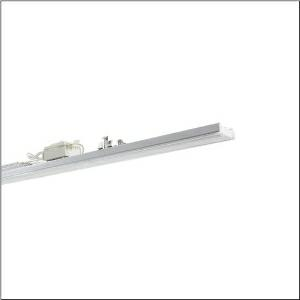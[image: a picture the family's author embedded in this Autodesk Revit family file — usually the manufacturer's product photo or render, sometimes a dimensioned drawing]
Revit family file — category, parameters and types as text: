
# Revit family: licross_21_recessed_ho_52tl11dn4e5s
name_source: partatom
category: Lighting Fixtures
units: mm (PartAtom-declared; Revit-internal decimal feet)

## family parameters
Cut with Voids When Loaded = No
Host = Face
Light Source = No
Part Type = Normal
Room Calculation Point = No
Round Connector Dimension = Use Diameter
Shared = No

## types (1)
- --- (1 x LED, 14970 lm, 84.6 W, 4000K)
    Apparent Load = 85 VA
    CIE Flux Codes = 87 95 99 100 100
    Color Rendering = 80
    Color Temperature = 4000K
    Default Elevation = 1800 mm
    Description = Licross 21 Recessed HO, luminaire insert, of sheet steel, galvanised, coil coated, white, length: 1.500mm, width: 66mm, height: 67mm, LED rated luminous flux: 14.970lm, light colour: 840, SDCM (Standard Deviation of Colour Matching)MacAdam ≤ 3 SDCM (initial), control gear: DALI 2, with plug, 5-pole, with phase selection, mains connection: 220..240V, AC, 50/60Hz, rated input power: 85W, internal wiring halogen-free, primary light control with lens, of plastic, primary optical cover: cover, of PMMA, light emission: direct distribution, primary light characteristic: symmetric, protection rating (complete): IP40, insulation class (complete): insulation class I (protective earthing), certification: CE, ENEC, VDE, UKCA, protection symbol: D if used in an environment without relevant dust loads with corresponding accessories, impact resistance: IK06, permissible ambient temperature for indoor applications: -25..+30°C, corresponds to IFS (International Featured Standards) requirements for safety and quality in the food industry, reducing of maximum allowable ambient temperature of 5°C with ceiling mounting, LABS conformity tested according to VDMA 24364:2018-05, The light source and the operating device comply with the requirements of the Ecodesign Regulation (EU) 2019/2020 and are replaceable in accordance with this regulation, packaging unit: 1 piece
    Height = 58 mm
    Lamp = 1 x LED
    Lamp Light Flux = 14970 lm
    Lamp Power = 84.6 W
    Lamp count = 1
    Length = 1500 mm
    Luminous efficacy = 177 lm/W
    Manufacturer = Siteco
    ModVariant = No
    Model = 52TL11DN4E5S
    Mounting Place = Ceiling
    Mounting Type = Pendant
    Number of Poles = 1
    OnlyDefault = Yes
    Power Factor = 1
    Product Name = Licross 21 Recessed HO
    Product group = luminaire insert | ceiling pendant
    ProductGroupID = 901
    Protection Class = Protection class I
    Protection Degree = IP 40
    RLX_Detail_Level = 1
    RLX_Emergency_Light_Flux = 0 lm
    RLX_Emergency_Type = 0
    RLX_Emergency_Type_DB = No
    RlxData = <blob elided: 24901 chars, md5=81b0afe6>
    Socket = socket
    Standby Power = 0 W
    System Light Flux = 14970 lm
    System Power = 85 W
    Type Comments = factory setting: luminous flux: 100 % | dim-lin: 254 | 484 mA
    Type Image = l_1296930.jpg
    URL = http://relux.com
    VarID = @adj_127461
    Voltage = 0 V
    Weight = 0.00 kg
    Width = 66 mm

## geometry (parser evidence)
native form markers: Blend x4, Sweep x13
no freeform markers — native parametric forms only
